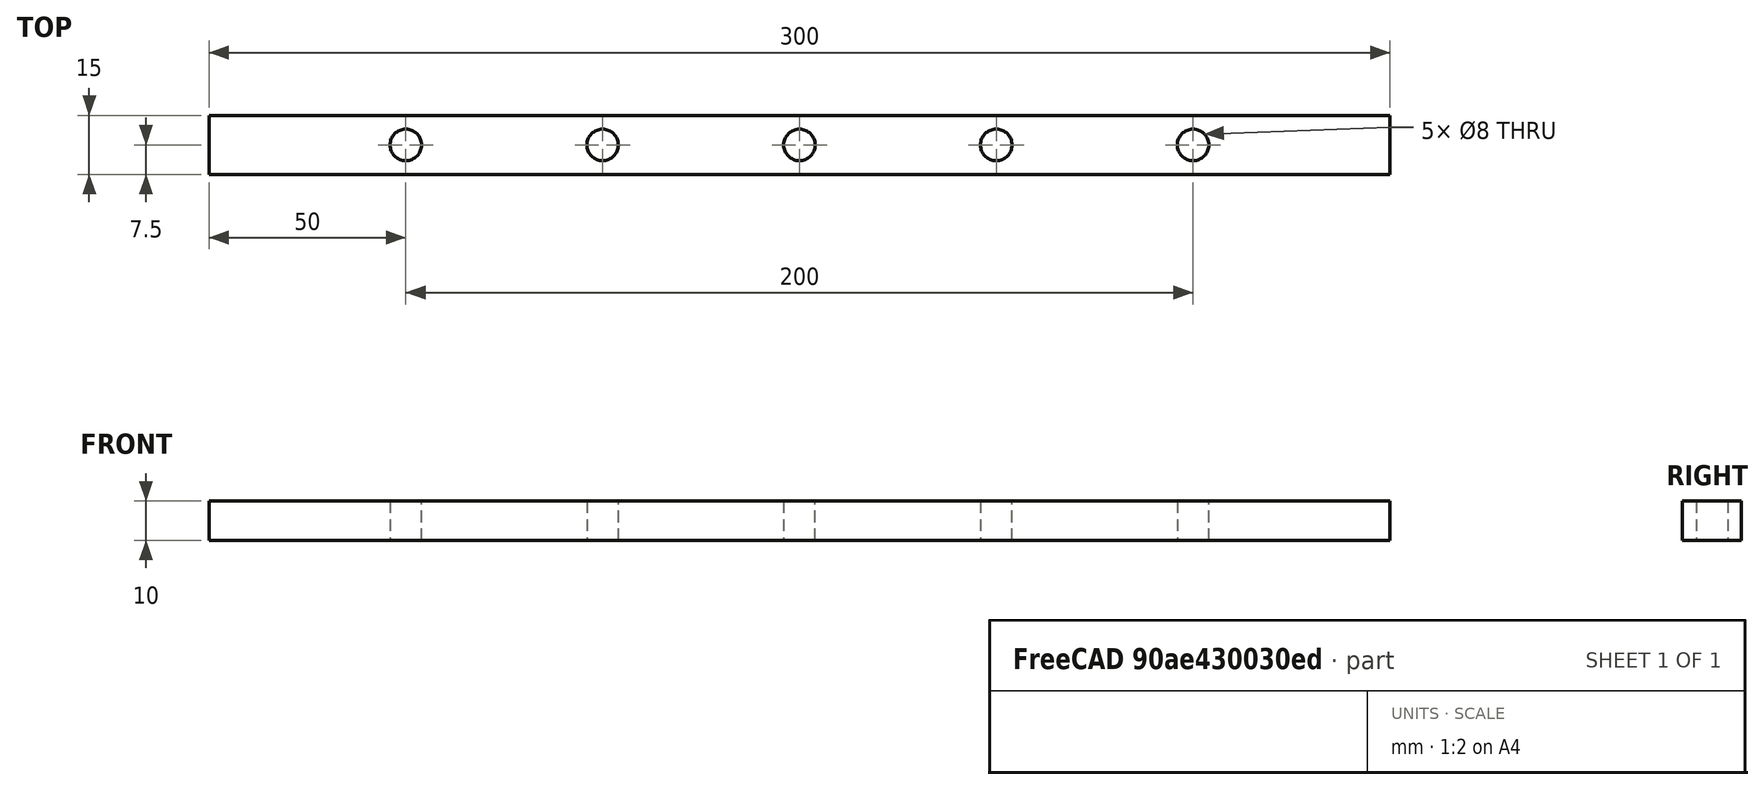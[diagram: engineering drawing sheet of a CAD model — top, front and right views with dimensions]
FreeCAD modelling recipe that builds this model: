
FCSTD DOCUMENT  (FreeCAD 0.19R24276 (Git))
Label: naprav_300x10x15
License: All rights reserved
LicenseURL: http://en.wikipedia.org/wiki/All_rights_reserved
objects: Sketcher::SketchObject×1, PartDesign::Pad×1, PartDesign::Body×1
note: 4 computed .brp shape members not serialized (recipe doc carries the construction recipe); baked Part::Feature solids carry a one-line shape summary decoded from their .brp

FEATURE [Sketcher::SketchObject] Sketch
  FullyConstrained = false
  MapMode = 5
  Support = -> [XY_Plane]
  sketch-geometry (9):
    g0: LineSegment StartX=0 StartY=15 StartZ=0 EndX=300 EndY=15 EndZ=0
    g1: LineSegment StartX=300 StartY=15 StartZ=0 EndX=300 EndY=0 EndZ=0
    g2: LineSegment StartX=300 StartY=0 StartZ=0 EndX=0 EndY=0 EndZ=0
    g3: LineSegment StartX=0 StartY=0 StartZ=0 EndX=0 EndY=15 EndZ=0
    g4: Circle CenterX=50 CenterY=7.5 CenterZ=0 NormalX=0 NormalY=0 NormalZ=1 AngleXU=0 Radius=4
    g5: Circle CenterX=100 CenterY=7.5 CenterZ=0 NormalX=0 NormalY=0 NormalZ=1 AngleXU=0 Radius=4
    g6: Circle CenterX=150 CenterY=7.5 CenterZ=0 NormalX=0 NormalY=0 NormalZ=1 AngleXU=0 Radius=4
    g7: Circle CenterX=200 CenterY=7.5 CenterZ=0 NormalX=0 NormalY=0 NormalZ=1 AngleXU=0 Radius=4
    g8: Circle CenterX=250 CenterY=7.5 CenterZ=0 NormalX=0 NormalY=0 NormalZ=1 AngleXU=0 Radius=4
  constraints (23):
    c: Coincident(g0,g1)
    c: Coincident(g1,g2)
    c: Coincident(g2,g3)
    c: Coincident(g3,g0)
    c: Horizontal(g0)
    c: Horizontal(g2)
    c: Vertical(g1)
    c: Vertical(g3)
    c: Coincident(g2,g-1)
    c: DistanceX(g2,g2) = 300
    c: DistanceY(g1,g1) = 15
    c: Diameter(g4) = 8
    c: Equal(g4,g5) = 8
    c: DistanceY(g2,g5) = 7.5
    c: DistanceY(g2,g6) = 7.5
    c: DistanceX(g0,g5) = 100
    c: DistanceX(g0,g6) = 150
    c: Diameter(g7) = 8
    c: DistanceX(g6,g7) = 50
    c: DistanceY(g7) = 7.5
    c: Diameter(g8) = 8
    c: DistanceY(g1,g8) = 7.5
    c: DistanceX(g0,g8) = 250
FEATURE [PartDesign::Pad] Pad
  Direction = (1,1,1)
  Length = 10
  Length2 = 100
  Profile = -> Sketch
  Type = 0
FEATURE [PartDesign::Body] Body
  Group = -> [Sketch,Pad]
  Origin = -> Origin
  Tip = -> Pad
